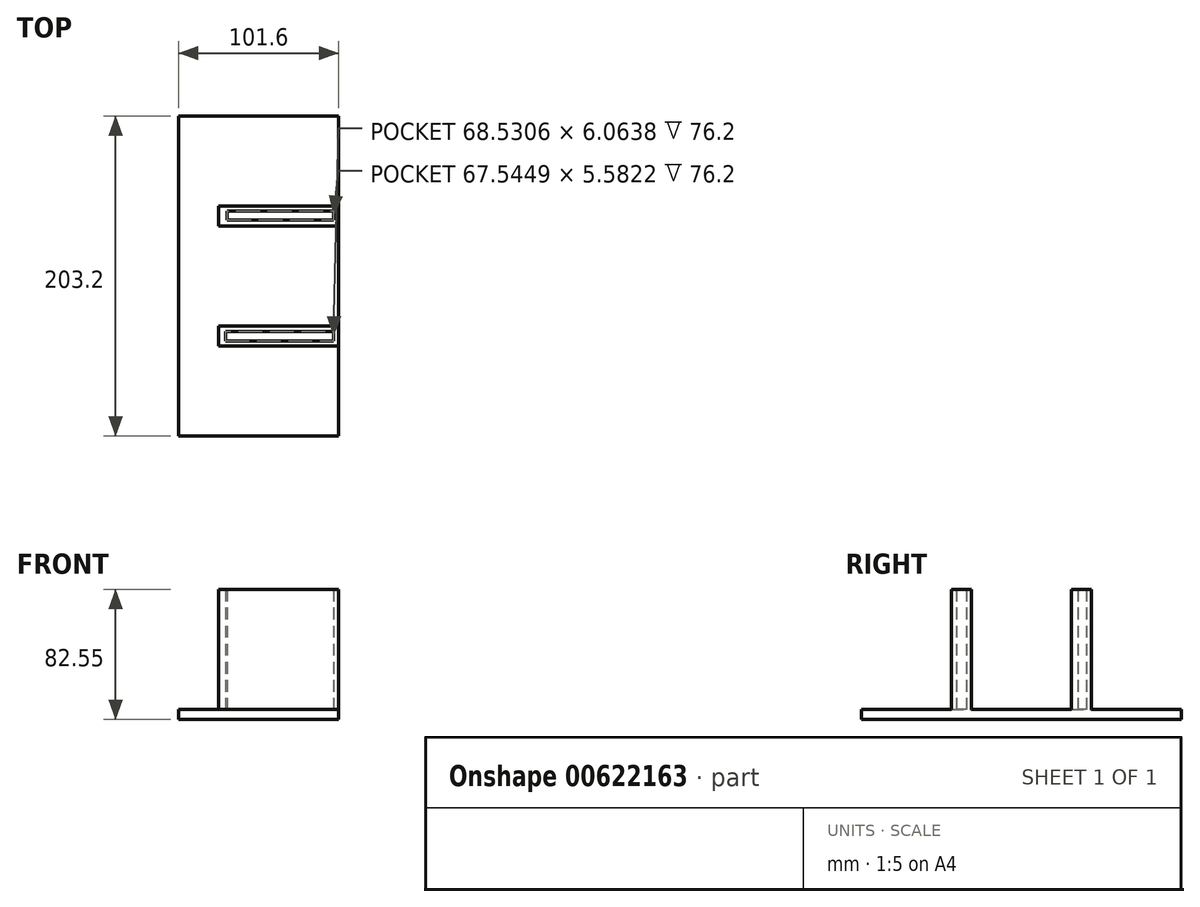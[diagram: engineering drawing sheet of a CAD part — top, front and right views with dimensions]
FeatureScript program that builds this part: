
annotation { "Feature Type Name" : "Feature", "Feature Type Description" : "" }
export const myFeature = defineFeature(function(context is Context, id is Id, definition is map)
    precondition{}
    {
        {
            var Q0;
            Q0=qCreatedBy(makeId("Top.planeOp"),FACE);
            var sketch = newSketch(context, id + "F0", { "sketchPlane" : qUnion([Q0])});
            skLineSegment(sketch, "E0.bottom", {"start": v(0, 0) * mm, "end": v(101.6, 0) * mm});
            skLineSegment(sketch, "E0.top", {"start": v(0, -203.2) * mm, "end": v(101.6, -203.2) * mm});
            skLineSegment(sketch, "E0.left", {"start": v(0, 0) * mm, "end": v(0, -203.2) * mm});
            skLineSegment(sketch, "E0.right", {"start": v(101.6, 0) * mm, "end": v(101.6, -203.2) * mm});
            skSolve(sketch);
        }
        {
            var Q0;
            Q0=makeQuery(id+"F0.imprint","IMPRINT",FACE,{"disambiguationData":[TD([[makeQuery(id+"F0.imprint","IMPRINT",EDGE,{"derivedFrom":sQuery(id+"F0.wireOp",EDGE,"E0.bottom")}),-1.0]])]});
            extrude(context, id + "F1", {"entities" : qUnion([Q0]), "depth" : 6.35 * mm, "offsetDistance" : 25.4 * mm});
        }
        {
            var Q0;
            Q0=makeQuery(id+"F1.opExtrude","CAP_FACE",FACE,{"disambiguationData":[OSD([sQuery(id+"F0.wireOp",EDGE,"E0.bottom"),sQuery(id+"F0.wireOp",EDGE,"E0.top"),sQuery(id+"F0.wireOp",EDGE,"E0.left"),sQuery(id+"F0.wireOp",EDGE,"E0.right")])],"isStart":false});
            var sketch = newSketch(context, id + "F2", { "sketchPlane" : qUnion([Q0])});
            skLineSegment(sketch, "E1.bottom", {"start": v(25.4, -146.05) * mm, "end": v(101.6, -146.05) * mm});
            skLineSegment(sketch, "E1.top", {"start": v(25.4, -133.35) * mm, "end": v(101.6, -133.35) * mm});
            skLineSegment(sketch, "E1.left", {"start": v(25.4, -146.05) * mm, "end": v(25.4, -133.35) * mm});
            skLineSegment(sketch, "E1.right", {"start": v(101.6, -146.05) * mm, "end": v(101.6, -133.35) * mm});
            skLineSegment(sketch, "E2.bottom", {"start": v(25.4, -69.85) * mm, "end": v(101.6, -69.85) * mm});
            skLineSegment(sketch, "E2.top", {"start": v(25.4, -57.15) * mm, "end": v(101.6, -57.15) * mm});
            skLineSegment(sketch, "E2.left", {"start": v(25.4, -69.85) * mm, "end": v(25.4, -57.15) * mm});
            skLineSegment(sketch, "E2.right", {"start": v(101.6, -69.85) * mm, "end": v(101.6, -57.15) * mm});
            skLineSegment(sketch, "E3.bottom", {"start": v(30.88, -60.32) * mm, "end": v(98.43, -60.32) * mm});
            skLineSegment(sketch, "E3.top", {"start": v(30.88, -65.9) * mm, "end": v(98.43, -65.9) * mm});
            skLineSegment(sketch, "E3.left", {"start": v(30.88, -60.32) * mm, "end": v(30.88, -65.9) * mm});
            skLineSegment(sketch, "E3.right", {"start": v(98.43, -60.33) * mm, "end": v(98.43, -65.9) * mm});
            skLineSegment(sketch, "E4.bottom", {"start": v(29.9, -136.81) * mm, "end": v(98.42, -136.81) * mm});
            skLineSegment(sketch, "E4.top", {"start": v(29.9, -142.87) * mm, "end": v(98.42, -142.87) * mm});
            skLineSegment(sketch, "E4.left", {"start": v(29.9, -136.81) * mm, "end": v(29.9, -142.87) * mm});
            skLineSegment(sketch, "E4.right", {"start": v(98.42, -136.81) * mm, "end": v(98.42, -142.87) * mm});
            skSolve(sketch);
        }
        {
            var Q0;
            Q0=makeQuery(id+"F2.imprint","IMPRINT",FACE,{"disambiguationData":[TD([[makeQuery(id+"F2.imprint","IMPRINT",EDGE,{"derivedFrom":sQuery(id+"F2.wireOp",EDGE,"E2.bottom")}),1.0]])]});
            var Q1;
            Q1=makeQuery(id+"F2.imprint","IMPRINT",FACE,{"disambiguationData":[TD([[makeQuery(id+"F2.imprint","IMPRINT",EDGE,{"derivedFrom":sQuery(id+"F2.wireOp",EDGE,"E1.bottom")}),1.0]])]});
            extrude(context, id + "F3", {"entities" : qUnion([Q0, Q1]), "operationType" : NewBodyOperationType.ADD, "depth" : 76.2 * mm, "offsetDistance" : 25.4 * mm});
        }
    });
